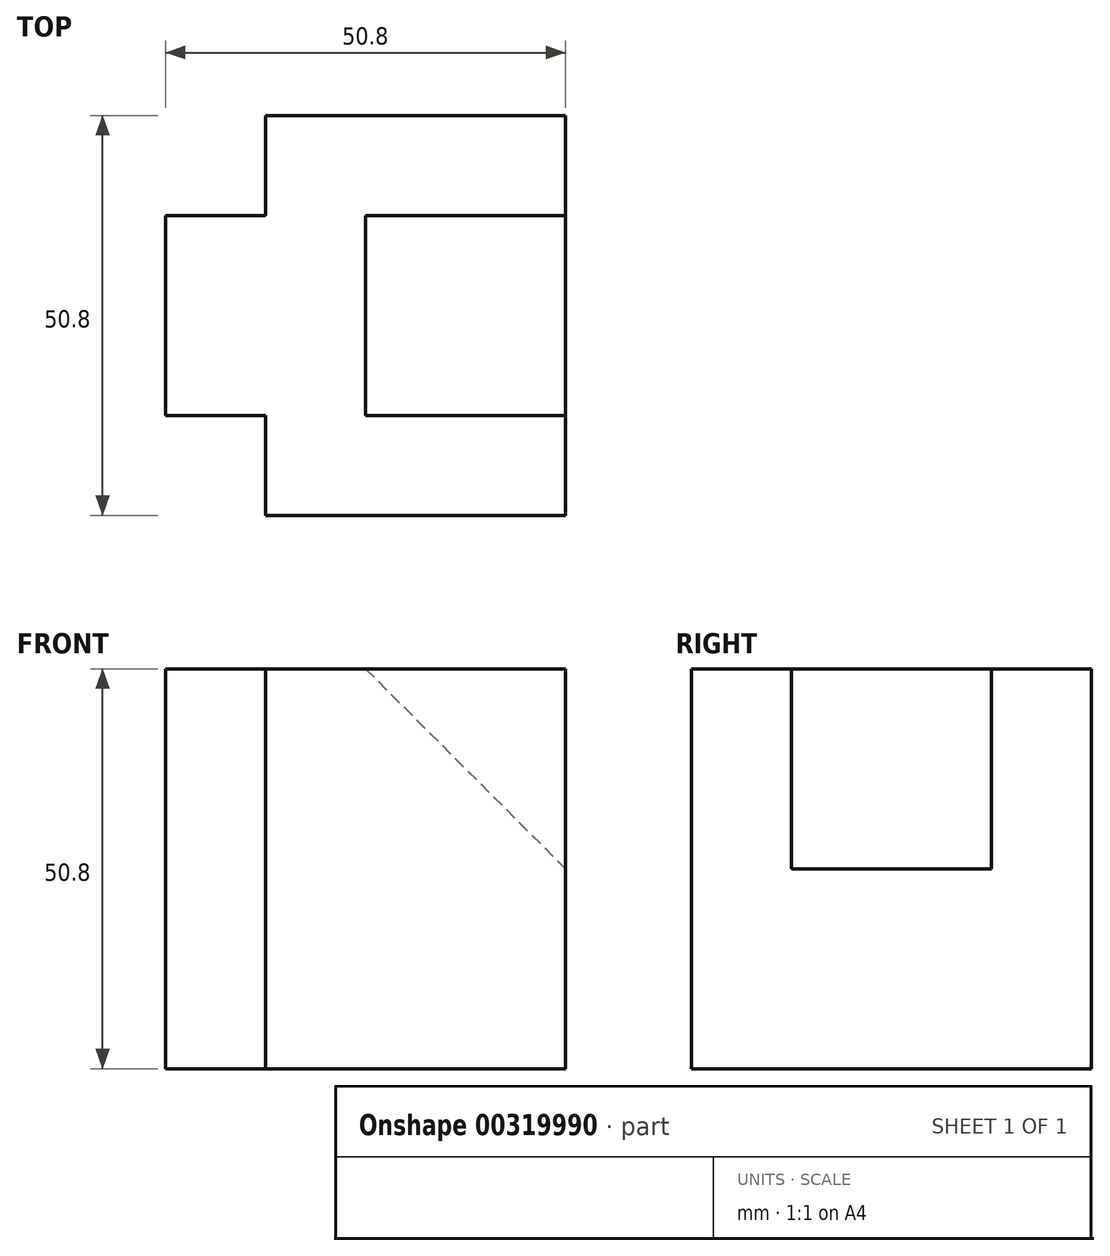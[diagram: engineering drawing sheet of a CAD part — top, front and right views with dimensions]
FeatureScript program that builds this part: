
annotation { "Feature Type Name" : "Feature", "Feature Type Description" : "" }
export const myFeature = defineFeature(function(context is Context, id is Id, definition is map)
    precondition{}
    {
        {
            var Q0;
            Q0=qCreatedBy(makeId("Top.planeOp"),FACE);
            var sketch = newSketch(context, id + "F0", { "sketchPlane" : qUnion([Q0])});
            skLineSegment(sketch, "E0", {"start": v(0, 12.7) * mm, "end": v(0, -12.7) * mm});
            skLineSegment(sketch, "E1", {"start": v(0, 12.7) * mm, "end": v(12.7, 12.7) * mm});
            skLineSegment(sketch, "E2", {"start": v(12.7, 12.7) * mm, "end": v(12.7, 25.4) * mm});
            skLineSegment(sketch, "E3", {"start": v(12.7, 25.4) * mm, "end": v(50.8, 25.4) * mm});
            skLineSegment(sketch, "E4", {"start": v(50.8, -25.4) * mm, "end": v(12.7, -25.4) * mm});
            skLineSegment(sketch, "E5", {"start": v(12.7, -25.4) * mm, "end": v(12.7, -12.7) * mm});
            skLineSegment(sketch, "E6", {"start": v(12.7, -12.7) * mm, "end": v(0, -12.7) * mm});
            skLineSegment(sketch, "E7", {"start": v(50.8, 25.4) * mm, "end": v(50.8, -25.4) * mm});
            skSolve(sketch);
        }
        {
            var Q0;
            Q0 = qSketchRegion(id + "F0", true);
            extrude(context, id + "F1", {"entities" : qUnion([Q0]), "depth" : 50.8 * mm});
        }
        {
            var Q0;
            Q0=qCreatedBy(makeId("Front.planeOp"),FACE);
            var sketch = newSketch(context, id + "F2", { "sketchPlane" : qUnion([Q0])});
            skLineSegment(sketch, "E8", {"start": v(25.4, 50.8) * mm, "end": v(50.8, 25.4) * mm});
            skLineSegment(sketch, "E9", {"start": v(50.8, 25.4) * mm, "end": v(50.8, 50.8) * mm});
            skLineSegment(sketch, "E10", {"start": v(50.8, 50.8) * mm, "end": v(25.4, 50.8) * mm});
            skSolve(sketch);
        }
        {
            var Q0;
            Q0 = qSketchRegion(id + "F2", true);
            extrude(context, id + "F3", {"entities" : qUnion([Q0]), "operationType" : NewBodyOperationType.REMOVE, "oppositeDirection" : true, "depth" : 12.7 * mm, "hasSecondDirection" : true, "secondDirectionOppositeDirection" : false, "secondDirectionDepth" : 12.7 * mm});
        }
    });
